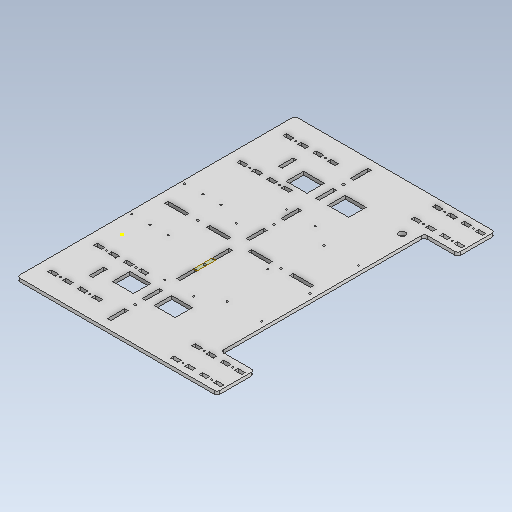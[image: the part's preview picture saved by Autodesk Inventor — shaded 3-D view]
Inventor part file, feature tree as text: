
AUTODESK INVENTOR PART (.ipt)
format: ipt  version: 2021.1 (Build 251245010, 245A)  size: 588,288 bytes
history: native  units: mm
features: reference x52, other x8, sketch x6, extrude x5
ambient origin geometry x8: Origin, YZ Plane, XZ Plane, XY Plane, X Axis, Y Axis, Z Axis, Center Point
bodies: Body1 (feature_tree)
feature tree (71):
  other  "РабПлоскость1"
  extrude  "Корпус"  Depth=6.0mm
  extrude  "Отверстия"  Depth=6.0mm
  extrude  "Выдавливание5"  TaperAngle=0.0deg  [1 undecoded]
  extrude  "Выдавливание6"  Depth=4.0mm
  sketch  "Эскиз8"
  extrude  "Выдавливание7"  Depth=6.0mm
  sketch  "Эскиз2"
  reference  "Ссылка16"
  reference  "Ссылка17"
  reference  "Ссылка18"
  reference  "Ссылка19"
  reference  "Ссылка20"
  reference  "Ссылка21"
  reference  "Ссылка22"
  reference  "Ссылка23"
  reference  "Ссылка24"
  reference  "Ссылка25"
  reference  "Ссылка26"
  reference  "Ссылка27"
  reference  "Ссылка28"
  reference  "Ссылка29"
  reference  "Ссылка30"
  reference  "Ссылка31"
  sketch  "Эскиз3"
  reference  "Ссылка32"
  reference  "Ссылка33"
  reference  "Ссылка34"
  reference  "Ссылка35"
  reference  "Ссылка36"
  reference  "Ссылка37"
  reference  "Ссылка38"
  reference  "Ссылка39"
  reference  "Ссылка40"
  reference  "Ссылка41"
  reference  "Ссылка42"
  reference  "Ссылка43"
  sketch  "Эскиз6"
  reference  "Ссылка52"
  reference  "Ссылка53"
  reference  "Ссылка54"
  sketch  "Эскиз7"
  reference  "Ссылка55"
  reference  "Ссылка57"
  reference  "Ссылка58"
  sketch  "Эскиз9"
  reference  "Ссылка59"
  reference  "Ссылка60"
  reference  "Ссылка61"
  reference  "Ссылка62"
  reference  "Ссылка63"
  reference  "Ссылка64"
  reference  "Ссылка65"
  reference  "Ссылка67"
  reference  "Ссылка68"
  reference  "Ссылка69"
  reference  "Ссылка70"
  reference  "Ссылка71"
  reference  "Ссылка72"
  reference  "Ссылка73"
  reference  "Ссылка74"
  reference  "Ссылка75"
  reference  "Ссылка76"
  reference  "Ссылка77"
  other  "<userpath>\Documents\Savka\3d\Korp.iam"
  other  "Korp.iam"
  other  "Korpus 2:1"
  other  "Korpus:1"
  other  "Korpus 5:1"
  other  "корпус:1"
  other  "Platforma_kolesa:1"
note: 1 required parameter value undecoded (feature->parameter linkage not recoverable at this tier; creation-order binding heuristic only, values carry confidence <= 0.55)
